# Revit family: 0047993
name_source: partatom
category: Lighting Fixtures
revit_build: Autodesk Revit 2016 (Build: 20150220_1215(x64)
units: mm (PartAtom-declared; Revit-internal decimal feet)

## family parameters
Cut with Voids When Loaded = No
Host = Face
Light Source = Yes
OmniClass Number = 23.80.70.00
OmniClass Title = Lighting
Part Type = Normal
Room Calculation Point = No
Round Connector Dimension = Use Diameter
Shared = No

## types (8) — shared parameters
Assembly Code = D5020200
AssetType = Fixed
BezelOffset_SYL = 30 mm
ClassificationName = Uniclass2015
ClassificationValue = EF_70_80
Color Filter = 16777215
Default Elevation = 1219 mm
DiffuserWidth_SYL = 546 mm  [stored 1.79134 ft]
Dimming Lamp Color Temperature Shift = <None>
DocumentationLiterature = http://www.sylvania-lighting.com
DurationUnit = hours
ElectricShockClassification = Class II
Emit Shape Visible in Rendering = No
Emit from Rectangle Length = 566 mm
Emit from Rectangle Width = 566 mm
ExpectedLife = 50000
IfcExportAs = IfcLightFixtureType
IfcExportType = IfcLightFixtureType
ImpactProtectionIndex = IK03
IngressProtection = IP44/20
Keynote = 16500
Lamp = LED
LampColourRenderingIndex = 80
LampColourTemperature = 4000 K
LampsType = LED
Length_SYL = 596 mm  [stored 1.95538 ft]
Manufacturer = Feilo Sylvania
ManufacturerName = Feilo Sylvania
Material = steel housing, pc diffuser
Material_1_SYL = Body-Sylvania-Start Panel LED DALI-White
Material_2_SYL = Diffuser-Sylvania-Start Panel LED DALI
Material_3_SYL = <By Category>
Material_4_SYL = <By Category>
Model = S Panel UGR19 600x600 IP44 Mltpwr 1625-4450Lm 840
ModelNumber = 0047993
ModelReference = S Panel UGR19 600x600 IP44 Mltpwr 1625-4450Lm 840
Name = S Panel UGR19 600x600 IP44 Mltpwr 1625-4450Lm 840
NominalDepth = 596 mm  [stored 1.95538 ft]
NominalHeight = 63 mm  [stored 0.206693 ft]
NominalLength = 596 mm  [stored 1.95538 ft]
PowerFactor = 0.95
Tilt Angle = -90.00°
Type Image = <None>
TypeName = S Panel UGR19 600x600 IP44 Mltpwr 1625-4450Lm 840
URL = http://www.sylvania-lighting.com
Voltage = 0 V
zero-valued in all types: Cost

## per-type parameters (varying)
| type | Apparent Load | LampNominalLuminous | LuminousEfficacy | Photometric Web File | PowerConsumption |
| 0047993 35W | 35 VA | 4553 lm | 129.3 lm/W | 0047993_35W.ies | 35 W |
| 0047993 32W | 32 VA | 4185 lm | 130.3 lm/W | 0047993_32W.ies | 32 W |
| 0047993 29W | 29 VA | 3776 lm | 131.1 lm/W | 0047993_29W.ies | 29 W |
| 0047993 26W | 26 VA | 3395 lm | 132.1 lm/W | 0047993_26W.ies | 26 W |
| 0047993 22W | 22 VA | 2896 lm | 132.2 lm/W | 0047993_22W.ies | 22 W |
| 0047993 19W | 19 VA | 2510 lm | 132.8 lm/W | 0047993_19W.ies | 19 W |
| 0047993 16W | 16 VA | 2056 lm | 131.8 lm/W | 0047993_16W.ies | 16 W |
| 0047993 13W | 13 VA | 1649 lm | 129.9 lm/W | 0047993_13W.ies | 13 W |

note: [stored X ft] marks values corroborated as IEEE doubles in the binary element streams (Revit-internal decimal feet)

## geometry (parser evidence)
native form markers: Sweep x1
no freeform markers — native parametric forms only
